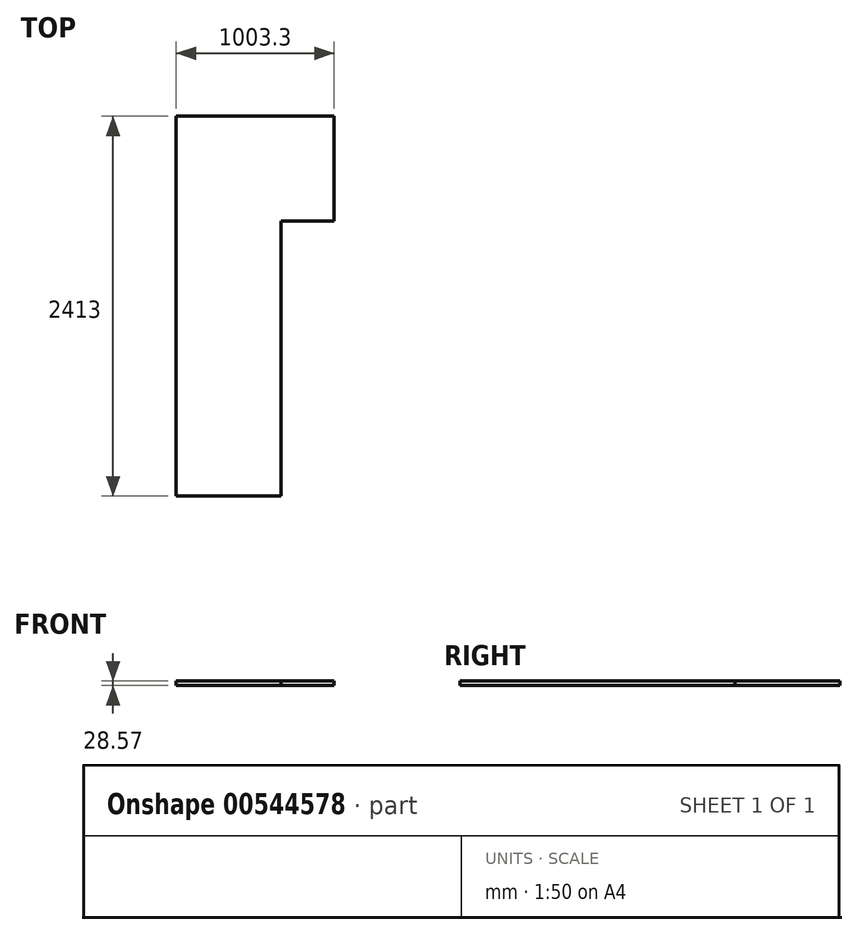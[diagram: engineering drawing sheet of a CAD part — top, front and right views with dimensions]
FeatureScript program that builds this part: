
annotation { "Feature Type Name" : "Feature", "Feature Type Description" : "" }
export const myFeature = defineFeature(function(context is Context, id is Id, definition is map)
    precondition{}
    {
        {
            var Q0;
            Q0=qCreatedBy(makeId("Top.planeOp"),FACE);
            var sketch = newSketch(context, id + "F0", { "sketchPlane" : qUnion([Q0])});
            skLineSegment(sketch, "E0", {"start": v(57.15, 0) * mm, "end": v(-946.15, 0) * mm});
            skLineSegment(sketch, "E1", {"start": v(-946.15, 0) * mm, "end": v(-946.15, -2413) * mm});
            skLineSegment(sketch, "E2", {"start": v(-946.15, -2393.95) * mm, "end": v(-304.8, -2393.95) * mm, "construction": true});
            skLineSegment(sketch, "E3", {"start": v(-304.8, -2393.95) * mm, "end": v(-304.8, -641.35) * mm, "construction": true});
            skLineSegment(sketch, "E4", {"start": v(-304.8, -641.35) * mm, "end": v(0, -641.35) * mm, "construction": true});
            skLineSegment(sketch, "E5.0", {"start": v(-946.15, -2413) * mm, "end": v(-279.4, -2413) * mm});
            skLineSegment(sketch, "E6.0", {"start": v(-279.4, -2413) * mm, "end": v(-279.4, -666.75) * mm});
            skLineSegment(sketch, "E7.0", {"start": v(-279.4, -666.75) * mm, "end": v(57.15, -666.75) * mm});
            skLineSegment(sketch, "E8.bottom", {"start": v(-863.6, -1060.45) * mm, "end": v(-393.7, -1060.45) * mm, "construction": true});
            skLineSegment(sketch, "E8.top", {"start": v(-863.6, -1803.4) * mm, "end": v(-393.7, -1803.4) * mm, "construction": true});
            skLineSegment(sketch, "E8.left", {"start": v(-863.6, -1060.45) * mm, "end": v(-863.6, -1803.4) * mm, "construction": true});
            skLineSegment(sketch, "E8.right", {"start": v(-393.7, -1060.45) * mm, "end": v(-393.7, -1803.4) * mm, "construction": true});
            skLineSegment(sketch, "E9", {"start": v(57.15, 0) * mm, "end": v(57.15, -666.75) * mm});
            skLineSegment(sketch, "E10", {"start": v(0, 0) * mm, "end": v(0, -641.35) * mm, "construction": true});
            skSolve(sketch);
        }
        {
            var Q0;
            Q0 = qSketchRegion(id + "F0", true);
            extrude(context, id + "F1", {"entities" : qUnion([Q0]), "depth" : 28.57 * mm, "offsetDistance" : 25.4 * mm});
        }
    });
